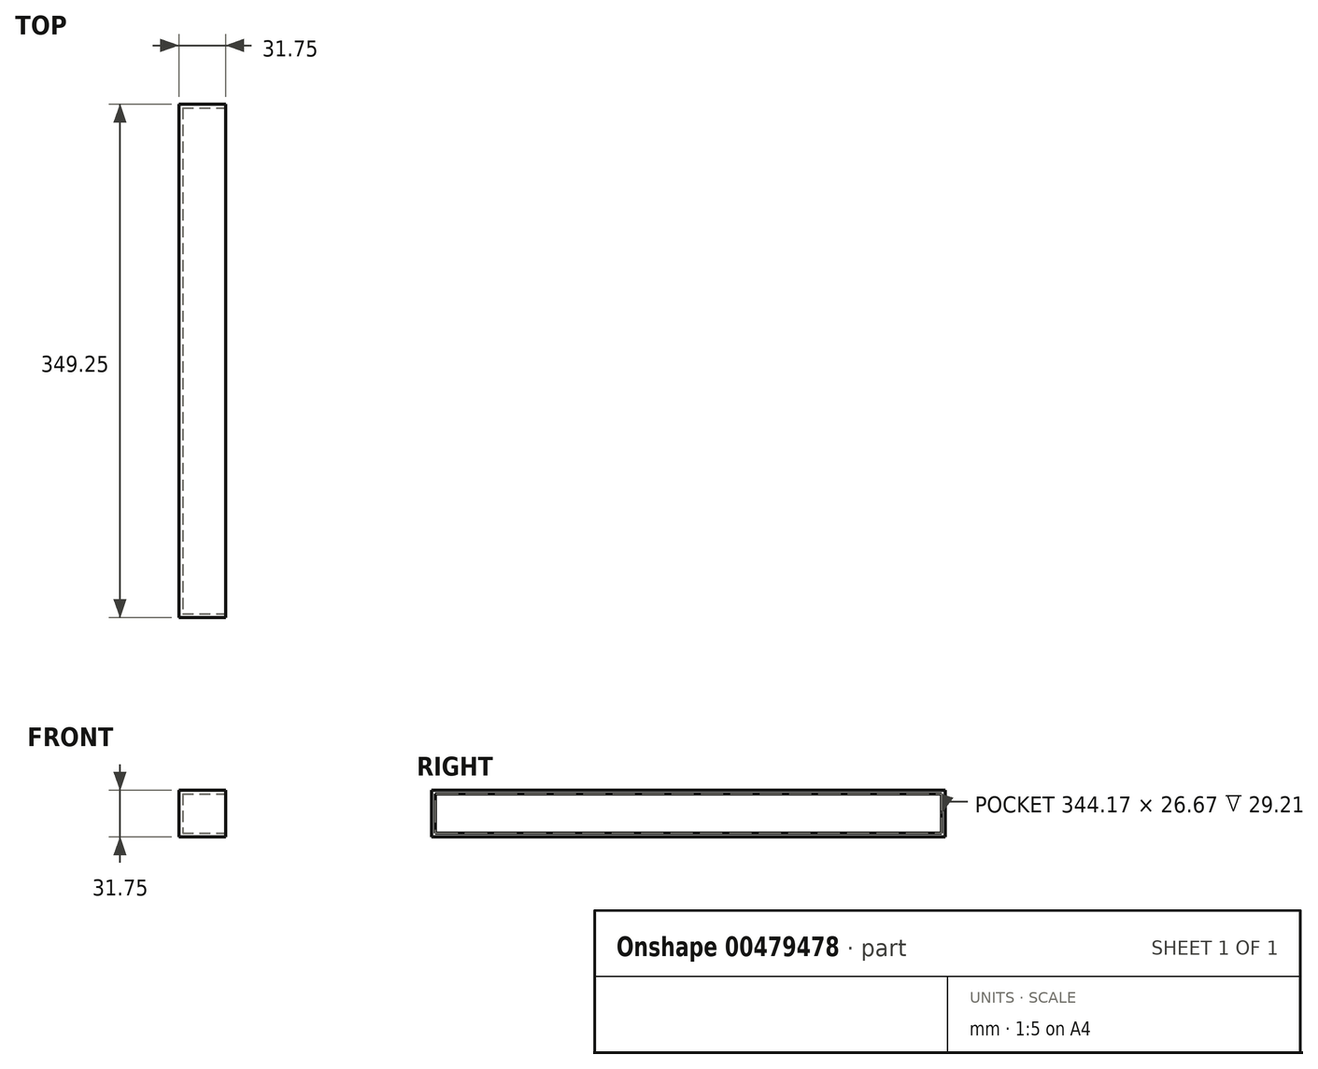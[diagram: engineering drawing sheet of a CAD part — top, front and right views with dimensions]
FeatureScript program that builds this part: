
annotation { "Feature Type Name" : "Feature", "Feature Type Description" : "" }
export const myFeature = defineFeature(function(context is Context, id is Id, definition is map)
    precondition{}
    {
        {
            var Q0;
            Q0=qCreatedBy(makeId("Top.planeOp"),FACE);
            var sketch = newSketch(context, id + "F0", { "sketchPlane" : qUnion([Q0])});
            skLineSegment(sketch, "E0.bottom", {"start": v(-81.09, 263.23) * mm, "end": v(-49.34, 263.23) * mm});
            skLineSegment(sketch, "E0.top", {"start": v(-81.09, -86.02) * mm, "end": v(-49.34, -86.02) * mm});
            skLineSegment(sketch, "E0.left", {"start": v(-81.09, 263.23) * mm, "end": v(-81.09, -86.02) * mm});
            skLineSegment(sketch, "E0.right", {"start": v(-49.34, 263.23) * mm, "end": v(-49.34, -86.02) * mm});
            skLineSegment(sketch, "E1.top", {"start": v(39.8, -88.46) * mm, "end": v(71.56, -88.46) * mm});
            skSolve(sketch);
        }
        {
            var Q0;
            Q0=makeQuery(id+"F0.imprint","IMPRINT",FACE,{"disambiguationData":[TD([[makeQuery(id+"F0.imprint","IMPRINT",EDGE,{"derivedFrom":sQuery(id+"F0.wireOp",EDGE,"E0.bottom")}),-1.0]])]});
            extrude(context, id + "F1", {"entities" : qUnion([Q0]), "depth" : 31.75 * mm});
        }
        {
            var Q0;
            Q0=makeQuery(id+"F1.opExtrude","SWEPT_FACE",FACE,{"disambiguationData":[OSD([sQuery(id+"F0.wireOp",EDGE,"E0.right")])]});
            shell(context, id + "F2", {"entities" : qUnion([Q0]), "thickness" : 2.54 * mm});
        }
    });
